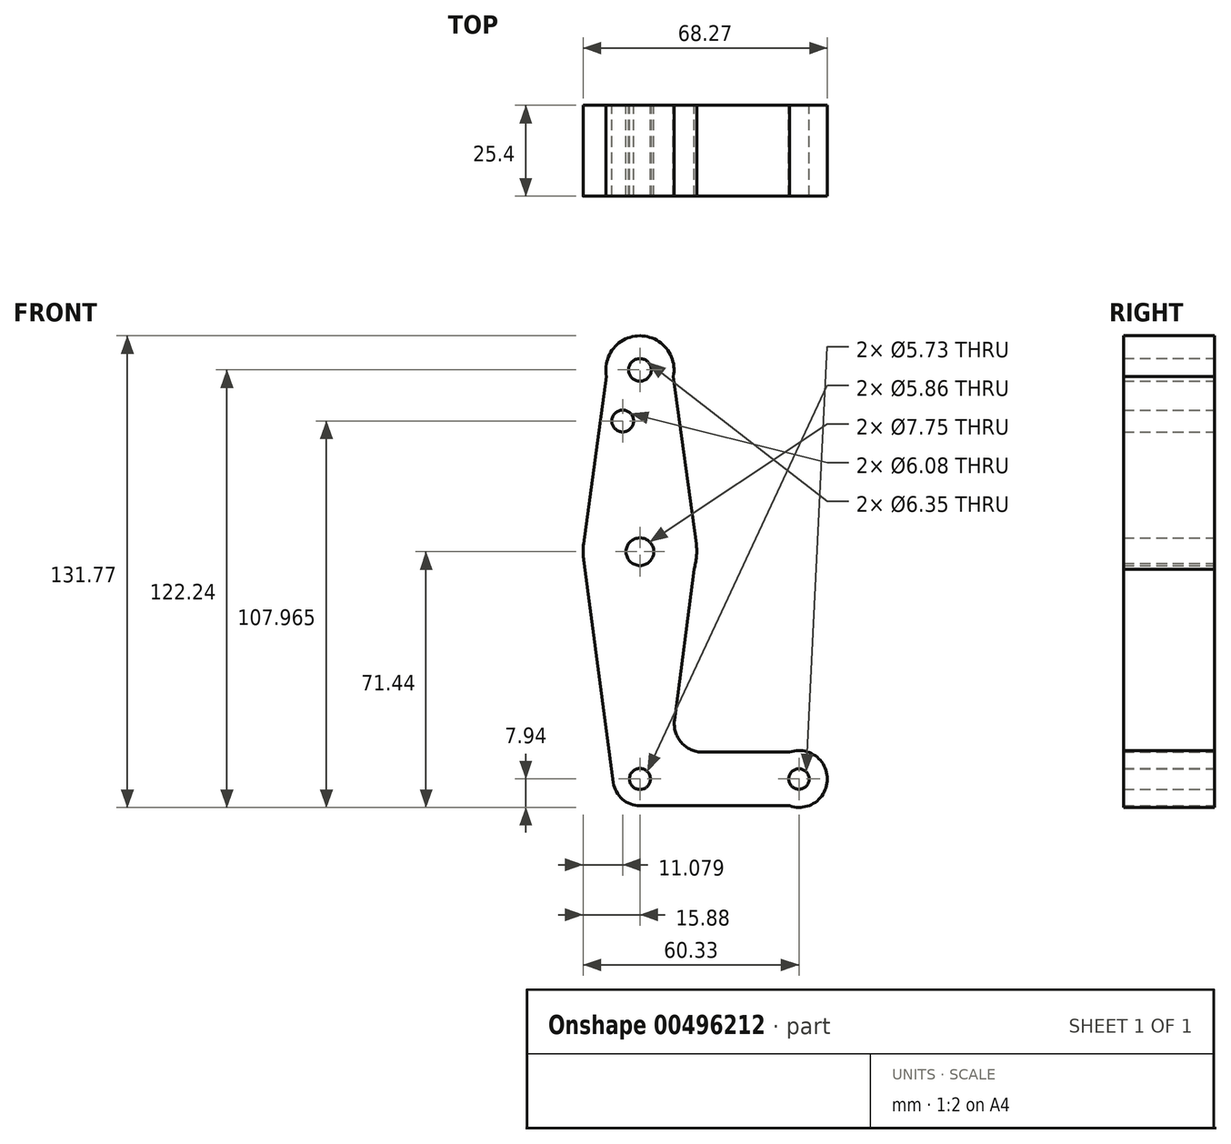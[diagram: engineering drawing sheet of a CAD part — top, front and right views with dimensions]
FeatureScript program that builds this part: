
annotation { "Feature Type Name" : "Feature", "Feature Type Description" : "" }
export const myFeature = defineFeature(function(context is Context, id is Id, definition is map)
    precondition{}
    {
        {
            var Q0;
            Q0=qCreatedBy(makeId("Front.planeOp"),FACE);
            var sketch = newSketch(context, id + "F0", { "sketchPlane" : qUnion([Q0])});
            skLineSegment(sketch, "E0", {"start": v(0, 114.3) * mm, "end": v(0, 7.49) * mm});
            skLineSegment(sketch, "E1", {"start": v(0, 0) * mm, "end": v(44.45, 0) * mm});
            skCircle(sketch, "E2", {"center": v(0, 114.3) * mm, "radius": 9.53 * mm});
            skCircle(sketch, "E3", {"center": v(44.45, 0) * mm, "radius": 7.94 * mm});
            skCircle(sketch, "E4", {"center": v(0, 63.5) * mm, "radius": 15.88 * mm});
            skLineSegment(sketch, "E5", {"start": v(8.5, 118.58) * mm, "end": v(15.73, 65.65) * mm});
            skLineSegment(sketch, "E6", {"start": v(-8.5, 118.58) * mm, "end": v(-15.73, 65.65) * mm});
            skLineSegment(sketch, "E7", {"start": v(15.1, 58.62) * mm, "end": v(9.67, 16.45) * mm});
            skLineSegment(sketch, "E8", {"start": v(-15.54, 60.27) * mm, "end": v(-7.42, -0.98) * mm});
            skLineSegment(sketch, "E9", {"start": v(17.55, 7.49) * mm, "end": v(47.1, 7.49) * mm});
            skCircle(sketch, "E10", {"center": v(-4.8, 100.03) * mm, "radius": 3.04 * mm});
            skCircle(sketch, "E11", {"center": v(0, 0) * mm, "radius": 2.93 * mm});
            skArc(sketch, "E12.filletArc", {"start": v(9.67, 16.45) * mm, "mid": v(11.58, 10.19) * mm, "end": v(17.55, 7.49) * mm});
            skCircle(sketch, "E13", {"center": v(0, 114.3) * mm, "radius": 3.18 * mm});
            skCircle(sketch, "E14", {"center": v(0, 0) * mm, "radius": 7.49 * mm});
            skPoint(sketch, "E15.start.orphan", {"position": v(0, -7.49) * mm});
            skCircle(sketch, "E16", {"center": v(44.45, 0) * mm, "radius": 2.86 * mm});
            skLineSegment(sketch, "E17", {"start": v(0, -7.49) * mm, "end": v(47.1, -7.49) * mm});
            skCircle(sketch, "E18", {"center": v(0, 63.5) * mm, "radius": 3.87 * mm});
            skSolve(sketch);
        }
        {
            var Q0;
            Q0 = qSketchRegion(id + "F0", true);
            extrude(context, id + "F1", {"entities" : qUnion([Q0]), "depth" : 25.4 * mm});
        }
        {
            var Q0;
            Q0 = qSketchRegion(id + "F0", true);
            extrude(context, id + "F2", {"entities" : qUnion([Q0]), "depth" : 25.4 * mm});
        }
    });
